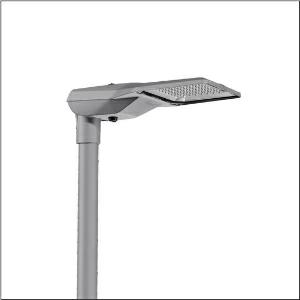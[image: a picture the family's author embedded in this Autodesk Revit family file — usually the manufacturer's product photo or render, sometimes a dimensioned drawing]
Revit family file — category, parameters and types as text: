
# Revit family: streetlight_sl_21_iq_midi___p1_0a_5xe3a31y08mb_7489
name_source: partatom
category: Lighting Fixtures
units: mm (PartAtom-declared; Revit-internal decimal feet)

## family parameters
Cut with Voids When Loaded = No
Host = Face
Light Source = No
Part Type = Normal
Room Calculation Point = No
Round Connector Dimension = Use Diameter
Shared = No

## types (1)
- --- (1 x LED, 18340 lm, 129.3 W, 3000K)
    Apparent Load = 129 VA
    CIE Flux Codes = 21 50 90 100 100
    Color Rendering = 70
    Color Temperature = 3000K
    Default Elevation = 1800 mm
    Description = Streetlight SL 21 iQ midi, mast luminaire, primary light control with lens, of PMMA, primary optical cover: cover, of toughened safety glass, transparent, light distribution: P1.0a, light emission: direct distribution, primary light characteristic: asymmetric, installation type: post-top, side-entry, LED, High Power LED, rated luminous flux: 18.340lm, luminous efficacy: 142lm/W, light colour: 730, colour temperature: 3000K, control: pre-setting: logarithmic dimming characteristic, Street-Remote, Auto-Match, Temp-Guard, Lumen-Switch, Night-Set, Smart-Wire, Light-Fading, Desk-Remote (wireless, voltage-free reading and setting of iQ features in the workshop via application-optimized NFC function/RFID function), optimised constant luminous flux control (CLO 2.0), mains connection: 230..240V, AC, 50/60Hz, start of lifetime: 129W, end of service life: 142W, reduction: 56W, luminaire housing, of diecast aluminium, powder-coated, Siteco® metallic grey (DB 702S), corrosivity category C5 mid according to DIN EN ISO 12944, please order mast flange separately, inclination adjustable: 0°, 5°, 10°, 15°, sealing non-destructively replaceable, multi-level sealing system, length: 644mm, width: 335mm, height: 110mm, mast flange for spigot size: 42mm (side-entry): 5XC10008XM4, 60/48mm (side-entry/post-top): 5XC10108XM2, 76/60mm (side-entry/post-top): 5XC10108XM1, Smart Interface below and above, protection rating (complete): IP66, insulation class (complete): insulation class II (safety insulation), certification: CE, ENEC, ENEC+, VDE, impact resistance: IK09, permissible operating ambient temperature for outdoor applications: -40..+50°C, standard-compliant lighting for roads and squares, packaging unit: 1 piece

Light Distribution: P1.0a
    Height = 111 mm
    Lamp = 1 x LED
    Lamp Light Flux = 18340 lm
    Lamp Power = 129.3 W
    Lamp count = 1
    Length = 644 mm
    Luminous efficacy = 142 lm/W
    Manufacturer = Siteco
    ModVariant = No
    Model = 5XE3A31Y08MB
    Number of Poles = 1
    OnlyDefault = Yes
    Power Factor = 1
    Product Name = Streetlight SL 21 iQ midi | P1.0a
    Product group = mast luminaire | pylon top
    ProductGroupID = 6100
    Protection Class = Protection class II
    Protection Degree = IP 66
    RLX_Detail_Level = 1
    RLX_Emergency_Light_Flux = 0 lm
    RLX_Emergency_Type = 0
    RLX_Emergency_Type_DB = No
    RlxData = <blob elided: 101853 chars, md5=0ad635ad>
    Socket = socket
    Standby Power = 0 W
    System Light Flux = 18340 lm
    System Power = 129 W
    Type Comments = factory setting: luminous flux: 100 % | dim-lin: 254 | 672 mA
    Type Image = l_1004304.jpg
    URL = http://relux.com
    VarID = @adj_082309
    Voltage = 0 V
    Weight = 0.00 kg
    Width = 336 mm

## geometry (parser evidence)
native form markers: Blend x4, Sweep x9
no freeform markers — native parametric forms only
